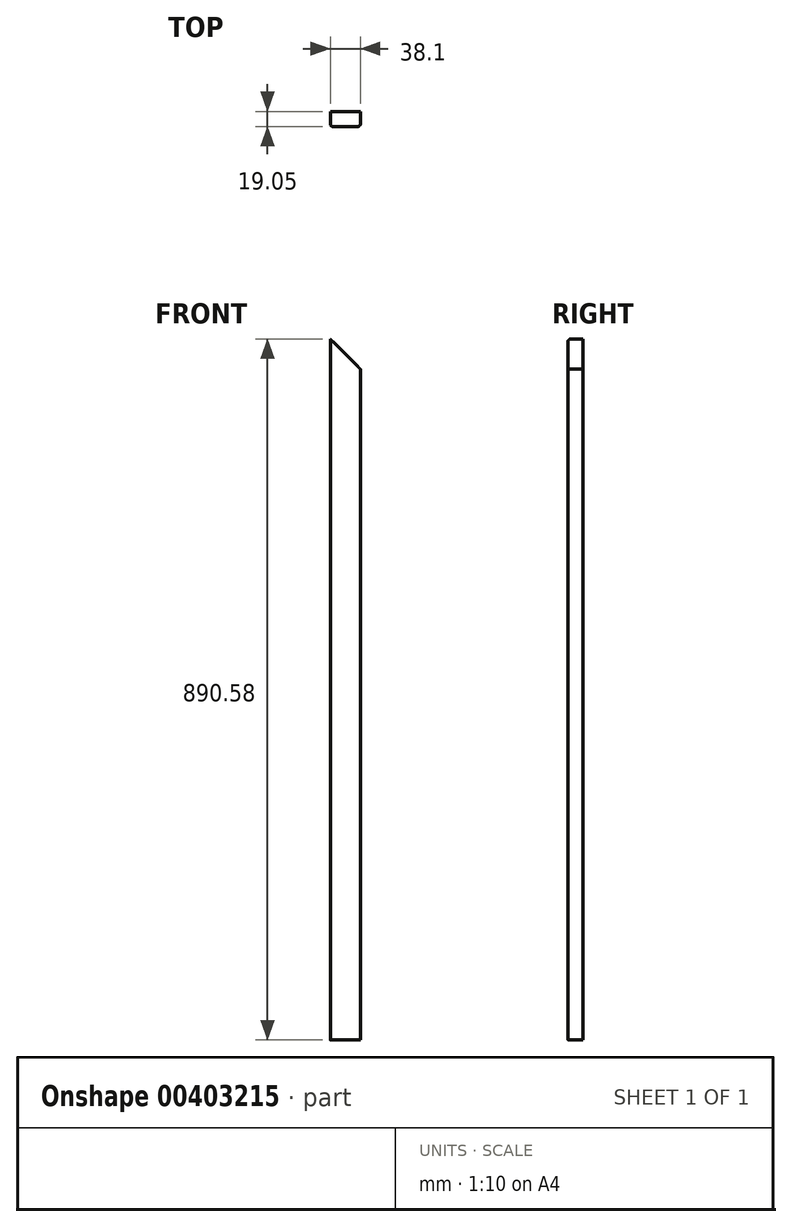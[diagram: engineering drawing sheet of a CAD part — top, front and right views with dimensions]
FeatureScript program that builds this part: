
annotation { "Feature Type Name" : "Feature", "Feature Type Description" : "" }
export const myFeature = defineFeature(function(context is Context, id is Id, definition is map)
    precondition{}
    {
        {
            var Q0;
            Q0=qCreatedBy(makeId("Front.planeOp"),FACE);
            var sketch = newSketch(context, id + "F0", { "sketchPlane" : qUnion([Q0])});
            skLineSegment(sketch, "E0.bottom", {"start": v(19.05, 445.3) * mm, "end": v(-19.05, 445.3) * mm});
            skLineSegment(sketch, "E0.top", {"start": v(19.05, -445.3) * mm, "end": v(-19.05, -445.3) * mm});
            skLineSegment(sketch, "E0.left", {"start": v(19.05, 445.3) * mm, "end": v(19.05, -445.3) * mm});
            skLineSegment(sketch, "E0.right", {"start": v(-19.05, 445.3) * mm, "end": v(-19.05, -445.3) * mm});
            skPoint(sketch, "E0.middle", {"position": v(0, 0) * mm});
            skSolve(sketch);
        }
        {
            var Q0;
            Q0=qSketchRegion(id+"F0",true);
            extrude(context, id + "F1", {"entities" : qUnion([Q0]), "depth" : 19.05 * mm});
        }
        {
            var Q0;
            Q0=makeQuery(id+"F1.opExtrude","CAP_FACE",FACE,{"disambiguationData":[OSD([sQuery(id+"F0.wireOp",EDGE,"E0.bottom"),sQuery(id+"F0.wireOp",EDGE,"E0.top"),sQuery(id+"F0.wireOp",EDGE,"E0.left"),sQuery(id+"F0.wireOp",EDGE,"E0.right")])],"isStart":false});
            var sketch = newSketch(context, id + "F2", { "sketchPlane" : qUnion([Q0])});
            skLineSegment(sketch, "E1", {"start": v(-19.05, 445.3) * mm, "end": v(19.05, 407.2) * mm});
            skLineSegment(sketch, "E2", {"start": v(19.05, 407.2) * mm, "end": v(19.05, 445.3) * mm});
            skLineSegment(sketch, "E3", {"start": v(19.05, 445.3) * mm, "end": v(-19.05, 445.3) * mm});
            skSolve(sketch);
        }
        {
            var Q0;
            Q0 = qSketchRegion(id + "F2", true);
            extrude(context, id + "F3", {"entities" : qUnion([Q0]), "operationType" : NewBodyOperationType.REMOVE, "endBound" : BoundingType.THROUGH_ALL, "oppositeDirection" : true, "depth" : 25.4 * mm});
        }
        {
            var Q0;
            Q0=makeQuery(id+"F1.opExtrude","CAP_EDGE",EDGE,{"disambiguationData":[OSD([sQuery(id+"F0.wireOp",EDGE,"E0.right")])],"isStart":false});
            var Q1;
            Q1=makeQuery(id+"F1.opExtrude","CAP_EDGE",EDGE,{"disambiguationData":[OSD([sQuery(id+"F0.wireOp",EDGE,"E0.left")])],"isStart":false});
            fillet(context, id + "F4", {"entities" : qUnion([Q0, Q1]), "radius" : 3.17 * mm, "tangentPropagation" : true, "allowEdgeOverflow" : false});
        }
    });
